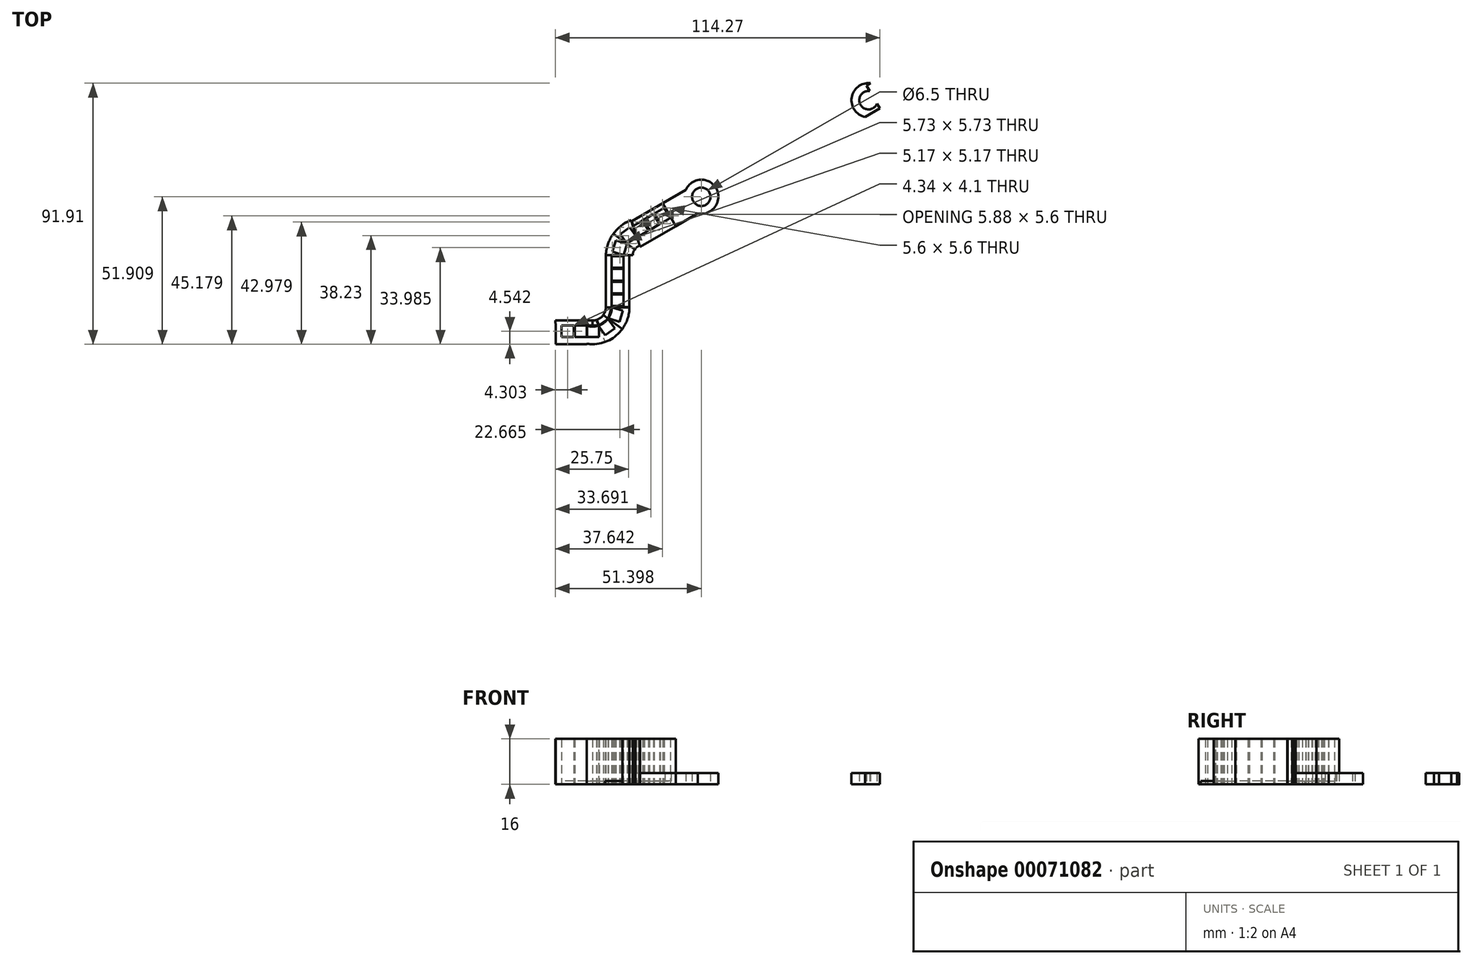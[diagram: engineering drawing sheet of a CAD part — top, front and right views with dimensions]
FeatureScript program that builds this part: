
annotation { "Feature Type Name" : "Feature", "Feature Type Description" : "" }
export const myFeature = defineFeature(function(context is Context, id is Id, definition is map)
    precondition{}
    {
        {
            var Q0;
            Q0=qCreatedBy(makeId("Top.planeOp"),FACE);
            var sketch = newSketch(context, id + "F0", { "sketchPlane" : qUnion([Q0])});
            skArc(sketch, "E0", {"start": v(-24.67, 35.72) * mm, "mid": v(-17.3, 34.42) * mm, "end": v(-13.22, 40.7) * mm});
            skLineSegment(sketch, "E1", {"start": v(-20, 40.64) * mm, "end": v(-26.78, 40.64) * mm});
            skLineSegment(sketch, "E2", {"start": v(-25.5, 44.6) * mm, "end": v(-26.77, 40.7) * mm});
            skLineSegment(sketch, "E3", {"start": v(-26.77, 40.7) * mm, "end": v(-30.67, 41.96) * mm});
            skLineSegment(sketch, "E4", {"start": v(-30.67, 41.96) * mm, "end": v(-29.4, 45.86) * mm});
            skLineSegment(sketch, "E5", {"start": v(-29.4, 45.86) * mm, "end": v(-25.5, 44.6) * mm});
            skArc(sketch, "E6", {"start": v(-23.08, 42.3) * mm, "mid": v(-20.83, 37.24) * mm, "end": v(-16.5, 40.7) * mm});
            skLineSegment(sketch, "E7", {"start": v(-30.9, 40.7) * mm, "end": v(-33, 40.7) * mm});
            skLineSegment(sketch, "E8.bottom", {"start": v(-26.8, 40.64) * mm, "end": v(-13.2, 40.64) * mm});
            skLineSegment(sketch, "E8.top", {"start": v(-26.8, 22.34) * mm, "end": v(-13.2, 22.34) * mm});
            skLineSegment(sketch, "E8.left", {"start": v(-26.8, 40.64) * mm, "end": v(-26.8, 22.34) * mm});
            skLineSegment(sketch, "E8.right", {"start": v(-13.2, 40.64) * mm, "end": v(-13.2, 22.34) * mm});
            skPoint(sketch, "E8.middle", {"position": v(-20, 31.5) * mm});
            skLineSegment(sketch, "E9.top", {"start": v(-30.9, 22.3) * mm, "end": v(-9.1, 22.3) * mm});
            skLineSegment(sketch, "E9.left", {"start": v(-30.9, 40.7) * mm, "end": v(-30.9, 22.3) * mm});
            skLineSegment(sketch, "E9.right", {"start": v(-9.1, 40.7) * mm, "end": v(-9.1, 22.3) * mm});
            skLineSegment(sketch, "E10.bottom", {"start": v(-26.8, 36.2) * mm, "end": v(-30.9, 36.2) * mm});
            skLineSegment(sketch, "E10.top", {"start": v(-26.8, 35.8) * mm, "end": v(-30.9, 35.8) * mm});
            skLineSegment(sketch, "E10.left", {"start": v(-26.8, 36.2) * mm, "end": v(-26.8, 35.8) * mm});
            skLineSegment(sketch, "E10.right", {"start": v(-30.9, 36.2) * mm, "end": v(-30.9, 35.8) * mm});
            skLineSegment(sketch, "E11.bottom", {"start": v(-26.8, 31.7) * mm, "end": v(-30.9, 31.7) * mm});
            skLineSegment(sketch, "E11.top", {"start": v(-26.8, 31.3) * mm, "end": v(-30.9, 31.3) * mm});
            skLineSegment(sketch, "E11.left", {"start": v(-26.8, 31.7) * mm, "end": v(-26.8, 31.3) * mm});
            skLineSegment(sketch, "E11.right", {"start": v(-30.9, 31.7) * mm, "end": v(-30.9, 31.3) * mm});
            skLineSegment(sketch, "E12.bottom", {"start": v(-26.8, 27.2) * mm, "end": v(-30.9, 27.2) * mm});
            skLineSegment(sketch, "E12.top", {"start": v(-26.8, 26.8) * mm, "end": v(-30.9, 26.8) * mm});
            skLineSegment(sketch, "E12.left", {"start": v(-26.8, 27.2) * mm, "end": v(-26.8, 26.8) * mm});
            skLineSegment(sketch, "E12.right", {"start": v(-30.9, 27.2) * mm, "end": v(-30.9, 26.8) * mm});
            skLineSegment(sketch, "E13.bottom", {"start": v(-26.8, 22.7) * mm, "end": v(-30.9, 22.7) * mm});
            skLineSegment(sketch, "E13.top", {"start": v(-26.8, 22.3) * mm, "end": v(-30.9, 22.3) * mm});
            skLineSegment(sketch, "E13.left", {"start": v(-26.8, 22.7) * mm, "end": v(-26.8, 22.3) * mm});
            skLineSegment(sketch, "E13.right", {"start": v(-30.9, 22.7) * mm, "end": v(-30.9, 22.3) * mm});
            skLineSegment(sketch, "E14", {"start": v(-30.9, 22.3) * mm, "end": v(-37.68, 22.3) * mm});
            skArc(sketch, "E15", {"start": v(-33, 27.22) * mm, "mid": v(-43.84, 19.43) * mm, "end": v(-30.9, 22.7) * mm});
            skLineSegment(sketch, "E16", {"start": v(-30.9, 22.3) * mm, "end": v(-32.12, 18.38) * mm});
            skLineSegment(sketch, "E17", {"start": v(-32.12, 18.38) * mm, "end": v(-28.21, 17.15) * mm});
            skLineSegment(sketch, "E18", {"start": v(-28.21, 17.15) * mm, "end": v(-26.98, 21.06) * mm});
            skLineSegment(sketch, "E19", {"start": v(-26.98, 21.06) * mm, "end": v(-30.9, 22.3) * mm});
            skLineSegment(sketch, "E20", {"start": v(-37.68, 22.3) * mm, "end": v(-27.16, 14.65) * mm});
            skLineSegment(sketch, "E21", {"start": v(-33, 40.7) * mm, "end": v(-33, 22.3) * mm});
            skArc(sketch, "E22.trimOffspring", {"start": v(-33, 34.42) * mm, "mid": v(-48.38, 14.92) * mm, "end": v(-24.68, 22.34) * mm});
            skArc(sketch, "E23.trimOffspring", {"start": v(-26.3, 28.84) * mm, "mid": v(-24.94, 28.18) * mm, "end": v(-23.5, 27.7) * mm});
            skLineSegment(sketch, "E24", {"start": v(-33, 40.3) * mm, "end": v(-26.8, 40.3) * mm});
            skLineSegment(sketch, "E25", {"start": v(-26.8, 40.64) * mm, "end": v(-33, 40.64) * mm});
            skArc(sketch, "E26.trimOffspring", {"start": v(-26.8, 40.68) * mm, "mid": v(-26.8, 40.64) * mm, "end": v(-26.8, 40.6) * mm});
            skLineSegment(sketch, "E27.trimOffspring", {"start": v(-23.5, 40.7) * mm, "end": v(-9.1, 40.7) * mm});
            skLineSegment(sketch, "E28", {"start": v(-20, 40.64) * mm, "end": v(-33, 40.7) * mm});
            skLineSegment(sketch, "E29", {"start": v(-20, 40.64) * mm, "end": v(-30.3, 48.13) * mm});
            skLineSegment(sketch, "E30", {"start": v(-23.5, 40.7) * mm, "end": v(-23.5, 22.3) * mm});
            skCircle(sketch, "E31", {"center": v(-37.68, 22.3) * mm, "radius": 4.68 * mm});
            skLineSegment(sketch, "E32", {"start": v(-20, 40.64) * mm, "end": v(-20.07, 22.3) * mm});
            skLineSegment(sketch, "E33", {"start": v(-37.68, 22.3) * mm, "end": v(-37.68, 15.5) * mm});
            skLineSegment(sketch, "E34", {"start": v(-37.64, 9.3) * mm, "end": v(-52.13, 9.3) * mm});
            skLineSegment(sketch, "E35", {"start": v(-50.68, 15.5) * mm, "end": v(-50.68, 9.3) * mm});
            skLineSegment(sketch, "E36.top", {"start": v(-39.78, 11.78) * mm, "end": v(-50.68, 11.78) * mm});
            skLineSegment(sketch, "E36.left", {"start": v(-39.78, 15.5) * mm, "end": v(-39.78, 11.78) * mm});
            skLineSegment(sketch, "E36.right", {"start": v(-50.68, 15.5) * mm, "end": v(-50.68, 11.78) * mm});
            skLineSegment(sketch, "E37.bottom", {"start": v(-43.88, 15.88) * mm, "end": v(-44.28, 15.88) * mm});
            skLineSegment(sketch, "E37.top", {"start": v(-43.88, 11.78) * mm, "end": v(-44.28, 11.78) * mm});
            skLineSegment(sketch, "E37.left", {"start": v(-43.88, 15.88) * mm, "end": v(-43.88, 11.78) * mm});
            skLineSegment(sketch, "E37.right", {"start": v(-44.28, 15.88) * mm, "end": v(-44.28, 11.78) * mm});
            skLineSegment(sketch, "E38.bottom", {"start": v(-49.02, 11.78) * mm, "end": v(-48.62, 11.78) * mm});
            skLineSegment(sketch, "E38.top", {"start": v(-49.02, 15.88) * mm, "end": v(-48.62, 15.88) * mm});
            skLineSegment(sketch, "E38.left", {"start": v(-49.02, 11.78) * mm, "end": v(-49.02, 15.88) * mm});
            skLineSegment(sketch, "E38.right", {"start": v(-48.62, 11.78) * mm, "end": v(-48.62, 15.88) * mm});
            skLineSegment(sketch, "E39", {"start": v(-37.68, 17.61) * mm, "end": v(-39.78, 17.61) * mm});
            skLineSegment(sketch, "E40", {"start": v(-39.78, 17.61) * mm, "end": v(-39.78, 9.3) * mm});
            skLineSegment(sketch, "E41", {"start": v(-37.68, 17.61) * mm, "end": v(-50.75, 17.61) * mm});
            skLineSegment(sketch, "E42", {"start": v(-50.75, 17.61) * mm, "end": v(-50.68, 15.5) * mm});
            skLineSegment(sketch, "E43", {"start": v(-35.42, 15.88) * mm, "end": v(-32.15, 18.35) * mm});
            skLineSegment(sketch, "E44", {"start": v(-35.42, 15.88) * mm, "end": v(-50.68, 15.88) * mm});
            skLineSegment(sketch, "E45.bottom", {"start": v(-35.46, 15.88) * mm, "end": v(-39.56, 15.88) * mm});
            skLineSegment(sketch, "E45.top", {"start": v(-35.46, 11.78) * mm, "end": v(-39.56, 11.78) * mm});
            skLineSegment(sketch, "E45.left", {"start": v(-35.46, 15.88) * mm, "end": v(-35.46, 11.78) * mm});
            skLineSegment(sketch, "E45.right", {"start": v(-39.56, 15.88) * mm, "end": v(-39.56, 11.78) * mm});
            skLineSegment(sketch, "E46", {"start": v(-36.2, 17.85) * mm, "end": v(-35.42, 15.88) * mm});
            skLineSegment(sketch, "E47", {"start": v(-35.42, 15.88) * mm, "end": v(-33.3, 10.05) * mm});
            skArc(sketch, "E48.trimOffspring", {"start": v(-20.05, 27.21) * mm, "mid": v(-10.8, 49.4) * mm, "end": v(-33, 40.2) * mm});
            skLineSegment(sketch, "E49", {"start": v(-20, 40.21) * mm, "end": v(-20, 53.21) * mm});
            skLineSegment(sketch, "E50", {"start": v(-24.68, 22.34) * mm, "end": v(-24.67, 40.64) * mm});
            skLineSegment(sketch, "E51", {"start": v(-20, 40.64) * mm, "end": v(-23.89, 52.62) * mm});
            skLineSegment(sketch, "E52", {"start": v(-25.5, 44.6) * mm, "end": v(-21.94, 46.63) * mm});
            skLineSegment(sketch, "E53", {"start": v(-23.08, 42.3) * mm, "end": v(63.52, 92.3) * mm});
            skLineSegment(sketch, "E54", {"start": v(-23.89, 52.62) * mm, "end": v(114.67, 132.62) * mm});
            skLineSegment(sketch, "E55", {"start": v(63.52, 92.3) * mm, "end": v(58.85, 100.39) * mm});
            skCircle(sketch, "E56", {"center": v(0.65, 61.2) * mm, "radius": 6 * mm});
            skCircle(sketch, "E57", {"center": v(0.65, 61.2) * mm, "radius": 3.25 * mm});
            skCircle(sketch, "E58", {"center": v(59.54, 95.2) * mm, "radius": 6 * mm});
            skCircle(sketch, "E59", {"center": v(59.54, 95.2) * mm, "radius": 3.25 * mm});
            skCircle(sketch, "E60", {"center": v(26.63, 76.2) * mm, "radius": 1.5 * mm});
            skLineSegment(sketch, "E61", {"start": v(-21.57, 47.22) * mm, "end": v(-10.05, 53.87) * mm});
            skLineSegment(sketch, "E62", {"start": v(-10.05, 53.87) * mm, "end": v(-8.3, 50.84) * mm});
            skLineSegment(sketch, "E63", {"start": v(-21.57, 47.22) * mm, "end": v(-23.62, 50.77) * mm});
            skLineSegment(sketch, "E64", {"start": v(-23.62, 50.77) * mm, "end": v(-12.1, 57.42) * mm});
            skLineSegment(sketch, "E65", {"start": v(-12.1, 57.42) * mm, "end": v(-10.05, 53.87) * mm});
            skLineSegment(sketch, "E66", {"start": v(-18.02, 49.27) * mm, "end": v(-20.07, 52.82) * mm});
            skLineSegment(sketch, "E67", {"start": v(-17.67, 49.47) * mm, "end": v(-19.72, 53.02) * mm});
            skLineSegment(sketch, "E68", {"start": v(-13.86, 51.67) * mm, "end": v(-15.9, 55.22) * mm});
            skLineSegment(sketch, "E69", {"start": v(-14.12, 51.52) * mm, "end": v(-16.17, 55.07) * mm});
            skLineSegment(sketch, "E70", {"start": v(-10.3, 53.72) * mm, "end": v(-12.36, 57.27) * mm});
            skLineSegment(sketch, "E71", {"start": v(-10.05, 53.87) * mm, "end": v(-12.1, 57.42) * mm});
            skLineSegment(sketch, "E72", {"start": v(-12.1, 57.42) * mm, "end": v(-12.97, 58.92) * mm});
            skSolve(sketch);
        }
        {
            var Q0;
            Q0=makeQuery(id+"F0.imprint","IMPRINT",FACE,{"disambiguationData":[TD([[makeQuery(id+"F0.imprint","IMPRINT",EDGE,{"derivedFrom":sQuery(id+"F0.wireOp",EDGE,"E2")}),1.0]])]});
            extrude(context, id + "F1", {"entities" : qUnion([Q0]), "depth" : 16 * mm, "offsetDistance" : 25 * mm});
        }
        {
            var Q0;
            {var subQ0=sQuery(id+"F0.wireOp",EDGE,"E9.left");var subQ13=sQuery(id+"F0.wireOp",EDGE,"E24");var subQ14=makeQuery(id+"F0.imprint","INTERSECT",VERTEX,{"derivedFrom":[subQ0,subQ13]});Q0=makeQuery(id+"F0.imprint","IMPRINT",FACE,{"disambiguationData":[TD([[makeQuery(id+"F0.imprint","IMPRINT",EDGE,{"disambiguationData":[TD([[subQ14,-1.0]])],"derivedFrom":subQ0}),-1.0]])]});}
            var Q1;
            {var subQ0=sQuery(id+"F0.wireOp",EDGE,"E8.left");var subQ16=makeQuery(id+"F0.imprint","INTERSECT",VERTEX,{"derivedFrom":[subQ0,sQuery(id+"F0.wireOp",EDGE,"E24")]});Q1=makeQuery(id+"F0.imprint","IMPRINT",FACE,{"disambiguationData":[TD([[makeQuery(id+"F0.imprint","IMPRINT",EDGE,{"disambiguationData":[TD([[subQ16,-1.0]])],"derivedFrom":subQ0}),1.0]])]});}
            var Q2;
            {var subQ4=sQuery(id+"F0.wireOp",EDGE,"E13.bottom");Q2=makeQuery(id+"F0.imprint","IMPRINT",FACE,{"disambiguationData":[TD([[makeQuery(id+"F0.imprint","IMPRINT",EDGE,{"derivedFrom":subQ4}),1.0]])]});}
            var Q3;
            {var subQ0=sQuery(id+"F0.wireOp",EDGE,"E24");var subQ1=sQuery(id+"F0.wireOp",EDGE,"E9.left");var subQ2=makeQuery(id+"F0.imprint","INTERSECT",VERTEX,{"derivedFrom":[subQ1,subQ0]});Q3=makeQuery(id+"F0.imprint","IMPRINT",FACE,{"disambiguationData":[TD([[makeQuery(id+"F0.imprint","IMPRINT",EDGE,{"disambiguationData":[TD([[subQ2,1.0]])],"derivedFrom":subQ1}),-1.0]])]});}
            var Q4;
            {var subQ0=sQuery(id+"F0.wireOp",EDGE,"E28");var subQ1=sQuery(id+"F0.wireOp",EDGE,"E9.left");var subQ2=makeQuery(id+"F0.imprint","INTERSECT",VERTEX,{"derivedFrom":[subQ1,subQ0]});Q4=makeQuery(id+"F0.imprint","IMPRINT",FACE,{"disambiguationData":[TD([[makeQuery(id+"F0.imprint","IMPRINT",EDGE,{"disambiguationData":[TD([[subQ2,-1.0]])],"derivedFrom":subQ1}),-1.0]])]});}
            var Q5;
            {var subQ0=sQuery(id+"F0.wireOp",EDGE,"2WVfRbEO-jWGe-ECgv-KHEP-8MCzaF3kxnAQ");var subQ1=sQuery(id+"F0.wireOp",EDGE,"E1");var subQ2=makeQuery(id+"F0.imprint","INTERSECT",VERTEX,{"derivedFrom":[subQ1,subQ0]});Q5=makeQuery(id+"F0.imprint","IMPRINT",FACE,{"disambiguationData":[TD([[makeQuery(id+"F0.imprint","IMPRINT",EDGE,{"disambiguationData":[TD([[subQ2,-1.0]])],"derivedFrom":subQ0}),1.0]])]});}
            var Q6;
            {var subQ0=sQuery(id+"F0.wireOp",EDGE,"E7");Q6=makeQuery(id+"F0.imprint","IMPRINT",FACE,{"disambiguationData":[TD([[makeQuery(id+"F0.imprint","IMPRINT",EDGE,{"derivedFrom":subQ0}),1.0]])]});}
            var Q7;
            {var subQ5=sQuery(id+"F0.wireOp",EDGE,"E53");var subQ7=sQuery(id+"F0.wireOp",EDGE,"E48.trimOffspring");var subQ8=makeQuery(id+"F0.imprint","INTERSECT",VERTEX,{"derivedFrom":[subQ7,subQ5]});Q7=makeQuery(id+"F0.imprint","IMPRINT",FACE,{"disambiguationData":[TD([[makeQuery(id+"F0.imprint","IMPRINT",EDGE,{"disambiguationData":[TD([[subQ8,-1.0]])],"derivedFrom":subQ7}),1.0]])]});}
            var Q8;
            {var subQ0=sQuery(id+"F0.wireOp",EDGE,"E72");Q8=makeQuery(id+"F0.imprint","IMPRINT",FACE,{"disambiguationData":[TD([[makeQuery(id+"F0.imprint","IMPRINT",EDGE,{"derivedFrom":subQ0}),1.0]])]});}
            var Q9;
            {var subQ0=sQuery(id+"F0.wireOp",EDGE,"E62");Q9=makeQuery(id+"F0.imprint","IMPRINT",FACE,{"disambiguationData":[TD([[makeQuery(id+"F0.imprint","IMPRINT",EDGE,{"derivedFrom":subQ0}),-1.0]])]});}
            var Q10;
            {var subQ0=sQuery(id+"F0.wireOp",EDGE,"E49");var subQ1=sQuery(id+"F0.wireOp",EDGE,"E48.trimOffspring");var subQ2=makeQuery(id+"F0.imprint","INTERSECT",VERTEX,{"derivedFrom":[subQ1,subQ0]});Q10=makeQuery(id+"F0.imprint","IMPRINT",FACE,{"disambiguationData":[TD([[makeQuery(id+"F0.imprint","IMPRINT",EDGE,{"disambiguationData":[TD([[subQ2,1.0]])],"derivedFrom":subQ0}),1.0]])]});}
            var Q11;
            {var subQ2=sQuery(id+"F0.wireOp",EDGE,"E66");Q11=makeQuery(id+"F0.imprint","IMPRINT",FACE,{"disambiguationData":[TD([[makeQuery(id+"F0.imprint","IMPRINT",EDGE,{"derivedFrom":subQ2}),-1.0]])]});}
            var Q12;
            {var subQ0=sQuery(id+"F0.wireOp",EDGE,"E65");Q12=makeQuery(id+"F0.imprint","IMPRINT",FACE,{"disambiguationData":[TD([[makeQuery(id+"F0.imprint","IMPRINT",EDGE,{"derivedFrom":subQ0}),-1.0]])]});}
            var Q13;
            {var subQ0=sQuery(id+"F0.wireOp",EDGE,"E68");var subQ1=sQuery(id+"F0.wireOp",EDGE,"E48.trimOffspring");var subQ2=makeQuery(id+"F0.imprint","INTERSECT",VERTEX,{"derivedFrom":[subQ1,subQ0]});Q13=makeQuery(id+"F0.imprint","IMPRINT",FACE,{"disambiguationData":[TD([[makeQuery(id+"F0.imprint","IMPRINT",EDGE,{"disambiguationData":[TD([[subQ2,-1.0]])],"derivedFrom":subQ1}),-1.0]])]});}
            var Q14;
            {var subQ0=sQuery(id+"F0.wireOp",EDGE,"E68");var subQ1=sQuery(id+"F0.wireOp",EDGE,"E48.trimOffspring");var subQ2=makeQuery(id+"F0.imprint","INTERSECT",VERTEX,{"derivedFrom":[subQ1,subQ0]});Q14=makeQuery(id+"F0.imprint","IMPRINT",FACE,{"disambiguationData":[TD([[makeQuery(id+"F0.imprint","IMPRINT",EDGE,{"disambiguationData":[TD([[subQ2,-1.0]])],"derivedFrom":subQ1}),1.0]])]});}
            var Q15;
            {var subQ6=sQuery(id+"F0.wireOp",EDGE,"E49");var subQ8=sQuery(id+"F0.wireOp",EDGE,"E61");var subQ10=makeQuery(id+"F0.imprint","INTERSECT",VERTEX,{"derivedFrom":[subQ6,subQ8]});Q15=makeQuery(id+"F0.imprint","IMPRINT",FACE,{"disambiguationData":[TD([[makeQuery(id+"F0.imprint","IMPRINT",EDGE,{"disambiguationData":[TD([[subQ10,1.0]])],"derivedFrom":subQ6}),1.0]])]});}
            var Q16;
            {var subQ7=sQuery(id+"F0.wireOp",EDGE,"E67");Q16=makeQuery(id+"F0.imprint","IMPRINT",FACE,{"disambiguationData":[TD([[makeQuery(id+"F0.imprint","IMPRINT",EDGE,{"derivedFrom":subQ7}),1.0]])]});}
            extrude(context, id + "F2", {"entities" : qUnion([Q0, Q1, Q2, Q3, Q4, Q5, Q6, Q7, Q8, Q9, Q10, Q11, Q12, Q13, Q14, Q15, Q16]), "depth" : 16 * mm, "offsetDistance" : 25 * mm});
        }
        {
            var Q0;
            {var subQ0=sQuery(id+"F0.wireOp",EDGE,"E10.bottom");Q0=makeQuery(id+"F0.imprint","IMPRINT",FACE,{"disambiguationData":[TD([[makeQuery(id+"F0.imprint","IMPRINT",EDGE,{"derivedFrom":subQ0}),1.0]])]});}
            var Q1;
            {var subQ2=sQuery(id+"F0.wireOp",EDGE,"E8.left");var subQ6=sQuery(id+"F0.wireOp",EDGE,"E24");var subQ7=makeQuery(id+"F0.imprint","INTERSECT",VERTEX,{"derivedFrom":[subQ2,subQ6]});Q1=makeQuery(id+"F0.imprint","IMPRINT",FACE,{"disambiguationData":[TD([[makeQuery(id+"F0.imprint","IMPRINT",EDGE,{"disambiguationData":[TD([[subQ7,1.0]])],"derivedFrom":subQ2}),-1.0]])]});}
            var Q2;
            {var subQ0=sQuery(id+"F0.wireOp",EDGE,"E11.bottom");Q2=makeQuery(id+"F0.imprint","IMPRINT",FACE,{"disambiguationData":[TD([[makeQuery(id+"F0.imprint","IMPRINT",EDGE,{"derivedFrom":subQ0}),1.0]])]});}
            var Q3;
            {var subQ0=sQuery(id+"F0.wireOp",EDGE,"E12.bottom");Q3=makeQuery(id+"F0.imprint","IMPRINT",FACE,{"disambiguationData":[TD([[makeQuery(id+"F0.imprint","IMPRINT",EDGE,{"derivedFrom":subQ0}),1.0]])]});}
            extrude(context, id + "F3", {"entities" : qUnion([Q0, Q1, Q2, Q3]), "depth" : 16 * mm, "offsetDistance" : 25 * mm});
        }
        {
            var Q0;
            {var subQ9=sQuery(id+"F0.wireOp",EDGE,"E17");Q0=makeQuery(id+"F0.imprint","IMPRINT",FACE,{"disambiguationData":[TD([[makeQuery(id+"F0.imprint","IMPRINT",EDGE,{"derivedFrom":subQ9}),-1.0]])]});}
            var Q1;
            {var subQ5=sQuery(id+"F0.wireOp",EDGE,"E16");Q1=makeQuery(id+"F0.imprint","IMPRINT",FACE,{"disambiguationData":[TD([[makeQuery(id+"F0.imprint","IMPRINT",EDGE,{"derivedFrom":subQ5}),-1.0]])]});}
            extrude(context, id + "F4", {"entities" : qUnion([Q0, Q1]), "depth" : 16 * mm, "offsetDistance" : 25 * mm});
        }
        {
            var Q0;
            Q0=makeQuery(id+"F1.opExtrude","SWEPT_BODY",BODY,{"disambiguationData":[OSD([sQuery(id+"F0.wireOp",EDGE,"E2"),sQuery(id+"F0.wireOp",EDGE,"E3"),sQuery(id+"F0.wireOp",EDGE,"E4"),sQuery(id+"F0.wireOp",EDGE,"E5"),sQuery(id+"F0.wireOp",EDGE,"E6"),sQuery(id+"F0.wireOp",EDGE,"E7"),sQuery(id+"F0.wireOp",EDGE,"E9.left"),sQuery(id+"F0.wireOp",EDGE,"E23.trimOffspring"),sQuery(id+"F0.wireOp",EDGE,"E28"),sQuery(id+"F0.wireOp",EDGE,"E29")])]});
            var Q1;
            Q1=makeQuery(id+"F1.opExtrude","SWEPT_FACE",FACE,{"disambiguationData":[OSD([sQuery(id+"F0.wireOp",EDGE,"E29")])]});
            mirror(context, id + "F5", {"entities" : qUnion([Q0]), "mirrorPlane" : qUnion([Q1])});
        }
        {
            var Q0;
            Q0=makeQuery(id+"F4.opExtrude","SWEPT_BODY",BODY,{"disambiguationData":[OSD([sQuery(id+"F0.wireOp",EDGE,"E9.top"),sQuery(id+"F0.wireOp",EDGE,"E14"),sQuery(id+"F0.wireOp",EDGE,"E15"),sQuery(id+"F0.wireOp",EDGE,"E16"),sQuery(id+"F0.wireOp",EDGE,"E17"),sQuery(id+"F0.wireOp",EDGE,"E18"),sQuery(id+"F0.wireOp",EDGE,"E19"),sQuery(id+"F0.wireOp",EDGE,"E20"),sQuery(id+"F0.wireOp",EDGE,"E22.trimOffspring"),sQuery(id+"F0.wireOp",EDGE,"E31")])]});
            var Q1;
            Q1=makeQuery(id+"F4.opExtrude","SWEPT_FACE",FACE,{"disambiguationData":[OSD([sQuery(id+"F0.wireOp",EDGE,"E20")])]});
            mirror(context, id + "F6", {"entities" : qUnion([Q0]), "mirrorPlane" : qUnion([Q1])});
        }
        {
            var Q0;
            {var subQ3=sQuery(id+"F0.wireOp",EDGE,"E40");var subQ5=sQuery(id+"F0.wireOp",EDGE,"E22.trimOffspring");var subQ7=makeQuery(id+"F0.imprint","INTERSECT",VERTEX,{"derivedFrom":[subQ5,subQ3]});Q0=makeQuery(id+"F0.imprint","IMPRINT",FACE,{"disambiguationData":[TD([[makeQuery(id+"F0.imprint","IMPRINT",EDGE,{"disambiguationData":[TD([[subQ7,1.0]])],"derivedFrom":subQ5}),1.0]])]});}
            var Q1;
            {var subQ2=sQuery(id+"F0.wireOp",EDGE,"E22.trimOffspring");var subQ8=sQuery(id+"F0.wireOp",EDGE,"E40");var subQ10=makeQuery(id+"F0.imprint","INTERSECT",VERTEX,{"derivedFrom":[subQ2,subQ8]});Q1=makeQuery(id+"F0.imprint","IMPRINT",FACE,{"disambiguationData":[TD([[makeQuery(id+"F0.imprint","IMPRINT",EDGE,{"disambiguationData":[TD([[subQ10,1.0]])],"derivedFrom":subQ2}),-1.0]])]});}
            var Q2;
            {var subQ3=sQuery(id+"F0.wireOp",EDGE,"E38.left");Q2=makeQuery(id+"F0.imprint","IMPRINT",FACE,{"disambiguationData":[TD([[makeQuery(id+"F0.imprint","IMPRINT",EDGE,{"derivedFrom":subQ3}),1.0]])]});}
            var Q3;
            {var subQ0=sQuery(id+"F0.wireOp",EDGE,"E42");Q3=makeQuery(id+"F0.imprint","IMPRINT",FACE,{"disambiguationData":[TD([[makeQuery(id+"F0.imprint","IMPRINT",EDGE,{"derivedFrom":subQ0}),1.0]])]});}
            var Q4;
            {var subQ0=sQuery(id+"F0.wireOp",EDGE,"E41");var subQ1=sQuery(id+"F0.wireOp",EDGE,"E15");var subQ2=makeQuery(id+"F0.imprint","INTERSECT",VERTEX,{"derivedFrom":[subQ1,subQ0]});Q4=makeQuery(id+"F0.imprint","IMPRINT",FACE,{"disambiguationData":[TD([[makeQuery(id+"F0.imprint","IMPRINT",EDGE,{"disambiguationData":[TD([[subQ2,-1.0]])],"derivedFrom":subQ1}),1.0]])]});}
            var Q5;
            {var subQ2=sQuery(id+"F0.wireOp",EDGE,"E37.left");Q5=makeQuery(id+"F0.imprint","IMPRINT",FACE,{"disambiguationData":[TD([[makeQuery(id+"F0.imprint","IMPRINT",EDGE,{"derivedFrom":subQ2}),-1.0]])]});}
            var Q6;
            {var subQ0=sQuery(id+"F0.wireOp",EDGE,"E38.left");Q6=makeQuery(id+"F0.imprint","IMPRINT",FACE,{"disambiguationData":[TD([[makeQuery(id+"F0.imprint","IMPRINT",EDGE,{"derivedFrom":subQ0}),-1.0]])]});}
            var Q7;
            {var subQ10=sQuery(id+"F0.wireOp",EDGE,"E36.left");Q7=makeQuery(id+"F0.imprint","IMPRINT",FACE,{"disambiguationData":[TD([[makeQuery(id+"F0.imprint","IMPRINT",EDGE,{"derivedFrom":subQ10}),1.0]])]});}
            var Q8;
            {var subQ5=sQuery(id+"F0.wireOp",EDGE,"E39");Q8=makeQuery(id+"F0.imprint","IMPRINT",FACE,{"disambiguationData":[TD([[makeQuery(id+"F0.imprint","IMPRINT",EDGE,{"derivedFrom":subQ5}),1.0]])]});}
            var Q9;
            {var subQ0=sQuery(id+"F0.wireOp",EDGE,"E41");var subQ1=sQuery(id+"F0.wireOp",EDGE,"E15");var subQ2=makeQuery(id+"F0.imprint","INTERSECT",VERTEX,{"derivedFrom":[subQ1,subQ0]});Q9=makeQuery(id+"F0.imprint","IMPRINT",FACE,{"disambiguationData":[TD([[makeQuery(id+"F0.imprint","IMPRINT",EDGE,{"disambiguationData":[TD([[subQ2,-1.0]])],"derivedFrom":subQ1}),-1.0]])]});}
            var Q10;
            {var subQ0=sQuery(id+"F0.wireOp",EDGE,"E38.top");var subQ1=sQuery(id+"F0.wireOp",EDGE,"E22.trimOffspring");var subQ2=makeQuery(id+"F0.imprint","INTERSECT",VERTEX,{"derivedFrom":[subQ1,subQ0]});Q10=makeQuery(id+"F0.imprint","IMPRINT",FACE,{"disambiguationData":[TD([[makeQuery(id+"F0.imprint","IMPRINT",EDGE,{"disambiguationData":[TD([[subQ2,-1.0]])],"derivedFrom":subQ1}),1.0]])]});}
            extrude(context, id + "F7", {"entities" : qUnion([Q0, Q1, Q2, Q3, Q4, Q5, Q6, Q7, Q8, Q9, Q10]), "operationType" : NewBodyOperationType.ADD, "depth" : 16 * mm, "offsetDistance" : 25 * mm});
        }
        {
            var Q0;
            {var subQ0=sQuery(id+"F0.wireOp",EDGE,"E46");Q0=makeQuery(id+"F0.imprint","IMPRINT",FACE,{"disambiguationData":[TD([[makeQuery(id+"F0.imprint","IMPRINT",EDGE,{"derivedFrom":subQ0}),-1.0]])]});}
            extrude(context, id + "F8", {"entities" : qUnion([Q0]), "depth" : 16 * mm, "offsetDistance" : 25 * mm});
        }
        {
            var Q0;
            {var subQ1=sQuery(id+"F0.wireOp",EDGE,"E48.trimOffspring");var subQ6=sQuery(id+"F0.wireOp",EDGE,"E53");var subQ7=makeQuery(id+"F0.imprint","INTERSECT",VERTEX,{"derivedFrom":[subQ1,subQ6]});Q0=makeQuery(id+"F0.imprint","IMPRINT",FACE,{"disambiguationData":[TD([[makeQuery(id+"F0.imprint","IMPRINT",EDGE,{"disambiguationData":[TD([[subQ7,-1.0]])],"derivedFrom":subQ1}),-1.0]])]});}
            var Q1;
            {var subQ0=sQuery(id+"F0.wireOp",EDGE,"E53");var subQ1=sQuery(id+"F0.wireOp",EDGE,"E48.trimOffspring");var subQ2=makeQuery(id+"F0.imprint","INTERSECT",VERTEX,{"derivedFrom":[subQ1,subQ0]});Q1=makeQuery(id+"F0.imprint","IMPRINT",FACE,{"disambiguationData":[TD([[makeQuery(id+"F0.imprint","IMPRINT",EDGE,{"disambiguationData":[TD([[subQ2,-1.0]])],"derivedFrom":subQ1}),1.0]])]});}
            var Q2;
            {var subQ4=sQuery(id+"F0.wireOp",EDGE,"E53");var subQ5=sQuery(id+"F0.wireOp",EDGE,"E49");var subQ6=makeQuery(id+"F0.imprint","INTERSECT",VERTEX,{"derivedFrom":[subQ5,subQ4]});Q2=makeQuery(id+"F0.imprint","IMPRINT",FACE,{"disambiguationData":[TD([[makeQuery(id+"F0.imprint","IMPRINT",EDGE,{"disambiguationData":[TD([[subQ6,-1.0]])],"derivedFrom":subQ5}),1.0]])]});}
            var Q3;
            {var subQ0=sQuery(id+"F0.wireOp",EDGE,"E56");var subQ3=makeQuery(id+"F0.imprint","IMPRINT",VERTEX,{"derivedFrom":subQ0});Q3=makeQuery(id+"F0.imprint","IMPRINT",FACE,{"disambiguationData":[TD([[makeQuery(id+"F0.imprint","IMPRINT",EDGE,{"disambiguationData":[TD([[subQ3,-1.0]])],"derivedFrom":subQ0}),-1.0]])]});}
            var Q4;
            {var subQ0=sQuery(id+"F0.wireOp",EDGE,"E55");var subQ8=sQuery(id+"F0.wireOp",EDGE,"E53");var subQ9=makeQuery(id+"F0.imprint","INTERSECT",VERTEX,{"derivedFrom":[subQ8,subQ0]});Q4=makeQuery(id+"F0.imprint","IMPRINT",FACE,{"disambiguationData":[TD([[makeQuery(id+"F0.imprint","IMPRINT",EDGE,{"disambiguationData":[TD([[subQ9,1.0]])],"derivedFrom":subQ8}),1.0]])]});}
            var Q5;
            Q5=makeQuery(id+"F0.imprint","IMPRINT",FACE,{"disambiguationData":[TD([[makeQuery(id+"F0.imprint","IMPRINT",EDGE,{"derivedFrom":sQuery(id+"F0.wireOp",EDGE,"E57")}),-1.0]])]});
            var Q6;
            {var subQ0=sQuery(id+"F0.wireOp",EDGE,"E56");var subQ1=sQuery(id+"F0.wireOp",EDGE,"E53");var subQ2=makeQuery(id+"F0.imprint","INTERSECT",VERTEX,{"disambiguationData":[OD(0.0)],"derivedFrom":[subQ1,subQ0]});Q6=makeQuery(id+"F0.imprint","IMPRINT",FACE,{"disambiguationData":[TD([[makeQuery(id+"F0.imprint","IMPRINT",EDGE,{"disambiguationData":[TD([[subQ2,1.0]])],"derivedFrom":subQ1}),-1.0]])]});}
            var Q7;
            {var subQ0=sQuery(id+"F0.wireOp",EDGE,"E56");var subQ1=sQuery(id+"F0.wireOp",EDGE,"E54");var subQ2=makeQuery(id+"F0.imprint","INTERSECT",VERTEX,{"disambiguationData":[OD(0.0)],"derivedFrom":[subQ1,subQ0]});Q7=makeQuery(id+"F0.imprint","IMPRINT",FACE,{"disambiguationData":[TD([[makeQuery(id+"F0.imprint","IMPRINT",EDGE,{"disambiguationData":[TD([[subQ2,-1.0]])],"derivedFrom":subQ1}),1.0]])]});}
            var Q8;
            {var subQ3=sQuery(id+"F0.wireOp",EDGE,"E59");var subQ5=makeQuery(id+"F0.imprint","IMPRINT",VERTEX,{"derivedFrom":subQ3});Q8=makeQuery(id+"F0.imprint","IMPRINT",FACE,{"disambiguationData":[TD([[makeQuery(id+"F0.imprint","IMPRINT",EDGE,{"disambiguationData":[TD([[subQ5,-1.0]])],"derivedFrom":subQ3}),-1.0]])]});}
            var Q9;
            {var subQ0=sQuery(id+"F0.wireOp",EDGE,"E58");var subQ1=sQuery(id+"F0.wireOp",EDGE,"E54");var subQ2=makeQuery(id+"F0.imprint","INTERSECT",VERTEX,{"disambiguationData":[OD(1.0)],"derivedFrom":[subQ1,subQ0]});Q9=makeQuery(id+"F0.imprint","IMPRINT",FACE,{"disambiguationData":[TD([[makeQuery(id+"F0.imprint","IMPRINT",EDGE,{"disambiguationData":[TD([[subQ2,-1.0]])],"derivedFrom":subQ1}),1.0]])]});}
            var Q10;
            {var subQ0=sQuery(id+"F0.wireOp",EDGE,"E62");Q10=makeQuery(id+"F0.imprint","IMPRINT",FACE,{"disambiguationData":[TD([[makeQuery(id+"F0.imprint","IMPRINT",EDGE,{"derivedFrom":subQ0}),1.0]])]});}
            var Q11;
            {var subQ0=sQuery(id+"F0.wireOp",EDGE,"E72");Q11=makeQuery(id+"F0.imprint","IMPRINT",FACE,{"disambiguationData":[TD([[makeQuery(id+"F0.imprint","IMPRINT",EDGE,{"derivedFrom":subQ0}),1.0]])]});}
            var Q12;
            {var subQ0=sQuery(id+"F0.wireOp",EDGE,"E49");var subQ1=sQuery(id+"F0.wireOp",EDGE,"E48.trimOffspring");var subQ2=makeQuery(id+"F0.imprint","INTERSECT",VERTEX,{"derivedFrom":[subQ1,subQ0]});Q12=makeQuery(id+"F0.imprint","IMPRINT",FACE,{"disambiguationData":[TD([[makeQuery(id+"F0.imprint","IMPRINT",EDGE,{"disambiguationData":[TD([[subQ2,1.0]])],"derivedFrom":subQ0}),1.0]])]});}
            var Q13;
            {var subQ3=sQuery(id+"F0.wireOp",EDGE,"E48.trimOffspring");var subQ5=sQuery(id+"F0.wireOp",EDGE,"E49");var subQ6=makeQuery(id+"F0.imprint","INTERSECT",VERTEX,{"derivedFrom":[subQ3,subQ5]});Q13=makeQuery(id+"F0.imprint","IMPRINT",FACE,{"disambiguationData":[TD([[makeQuery(id+"F0.imprint","IMPRINT",EDGE,{"disambiguationData":[TD([[subQ6,1.0]])],"derivedFrom":subQ3}),1.0]])]});}
            var Q14;
            {var subQ0=sQuery(id+"F0.wireOp",EDGE,"E56");var subQ1=sQuery(id+"F0.wireOp",EDGE,"E54");var subQ2=makeQuery(id+"F0.imprint","INTERSECT",VERTEX,{"disambiguationData":[OD(0.0)],"derivedFrom":[subQ1,subQ0]});Q14=makeQuery(id+"F0.imprint","IMPRINT",FACE,{"disambiguationData":[TD([[makeQuery(id+"F0.imprint","IMPRINT",EDGE,{"disambiguationData":[TD([[subQ2,1.0]])],"derivedFrom":subQ1}),1.0]])]});}
            extrude(context, id + "F9", {"entities" : qUnion([Q0, Q1, Q2, Q3, Q4, Q5, Q6, Q7, Q8, Q9, Q10, Q11, Q12, Q13, Q14]), "depth" : 4 * mm, "offsetDistance" : 25 * mm});
        }
        {
            var Q0;
            {var subQ5=sQuery(id+"F0.wireOp",EDGE,"E70");Q0=makeQuery(id+"F0.imprint","IMPRINT",FACE,{"disambiguationData":[TD([[makeQuery(id+"F0.imprint","IMPRINT",EDGE,{"derivedFrom":subQ5}),1.0]])]});}
            var Q1;
            {var subQ0=sQuery(id+"F0.wireOp",EDGE,"E67");Q1=makeQuery(id+"F0.imprint","IMPRINT",FACE,{"disambiguationData":[TD([[makeQuery(id+"F0.imprint","IMPRINT",EDGE,{"derivedFrom":subQ0}),-1.0]])]});}
            var Q2;
            {var subQ0=sQuery(id+"F0.wireOp",EDGE,"E69");var subQ1=sQuery(id+"F0.wireOp",EDGE,"E48.trimOffspring");var subQ2=makeQuery(id+"F0.imprint","INTERSECT",VERTEX,{"derivedFrom":[subQ1,subQ0]});Q2=makeQuery(id+"F0.imprint","IMPRINT",FACE,{"disambiguationData":[TD([[makeQuery(id+"F0.imprint","IMPRINT",EDGE,{"disambiguationData":[TD([[subQ2,-1.0]])],"derivedFrom":subQ1}),-1.0]])]});}
            var Q3;
            {var subQ0=sQuery(id+"F0.wireOp",EDGE,"E61");var subQ1=sQuery(id+"F0.wireOp",EDGE,"E49");var subQ2=makeQuery(id+"F0.imprint","INTERSECT",VERTEX,{"derivedFrom":[subQ1,subQ0]});Q3=makeQuery(id+"F0.imprint","IMPRINT",FACE,{"disambiguationData":[TD([[makeQuery(id+"F0.imprint","IMPRINT",EDGE,{"disambiguationData":[TD([[subQ2,-1.0]])],"derivedFrom":subQ1}),1.0]])]});}
            var Q4;
            {var subQ0=sQuery(id+"F0.wireOp",EDGE,"E61");var subQ1=sQuery(id+"F0.wireOp",EDGE,"E49");var subQ2=makeQuery(id+"F0.imprint","INTERSECT",VERTEX,{"derivedFrom":[subQ1,subQ0]});Q4=makeQuery(id+"F0.imprint","IMPRINT",FACE,{"disambiguationData":[TD([[makeQuery(id+"F0.imprint","IMPRINT",EDGE,{"disambiguationData":[TD([[subQ2,-1.0]])],"derivedFrom":subQ1}),-1.0]])]});}
            var Q5;
            {var subQ5=sQuery(id+"F0.wireOp",EDGE,"E29");var subQ7=sQuery(id+"F0.wireOp",EDGE,"E52");var subQ11=makeQuery(id+"F0.imprint","INTERSECT",VERTEX,{"derivedFrom":[subQ5,subQ7]});Q5=makeQuery(id+"F0.imprint","IMPRINT",FACE,{"disambiguationData":[TD([[makeQuery(id+"F0.imprint","IMPRINT",EDGE,{"disambiguationData":[TD([[subQ11,-1.0]])],"derivedFrom":subQ5}),-1.0]])]});}
            var Q6;
            Q6=makeQuery(id+"F0.imprint","IMPRINT",FACE,{"disambiguationData":[TD([[makeQuery(id+"F0.imprint","IMPRINT",EDGE,{"derivedFrom":sQuery(id+"F0.wireOp",EDGE,"E2")}),-1.0]])]});
            var Q7;
            {var subQ3=sQuery(id+"F0.wireOp",EDGE,"E10.bottom");Q7=makeQuery(id+"F0.imprint","IMPRINT",FACE,{"disambiguationData":[TD([[makeQuery(id+"F0.imprint","IMPRINT",EDGE,{"derivedFrom":subQ3}),-1.0]])]});}
            var Q8;
            {var subQ0=sQuery(id+"F0.wireOp",EDGE,"E10.top");Q8=makeQuery(id+"F0.imprint","IMPRINT",FACE,{"disambiguationData":[TD([[makeQuery(id+"F0.imprint","IMPRINT",EDGE,{"derivedFrom":subQ0}),1.0]])]});}
            var Q9;
            {var subQ0=sQuery(id+"F0.wireOp",EDGE,"E11.top");Q9=makeQuery(id+"F0.imprint","IMPRINT",FACE,{"disambiguationData":[TD([[makeQuery(id+"F0.imprint","IMPRINT",EDGE,{"derivedFrom":subQ0}),1.0]])]});}
            var Q10;
            {var subQ0=sQuery(id+"F0.wireOp",EDGE,"E12.top");Q10=makeQuery(id+"F0.imprint","IMPRINT",FACE,{"disambiguationData":[TD([[makeQuery(id+"F0.imprint","IMPRINT",EDGE,{"derivedFrom":subQ0}),1.0]])]});}
            var Q11;
            {var subQ3=sQuery(id+"F0.wireOp",EDGE,"E17");Q11=makeQuery(id+"F0.imprint","IMPRINT",FACE,{"disambiguationData":[TD([[makeQuery(id+"F0.imprint","IMPRINT",EDGE,{"derivedFrom":subQ3}),1.0]])]});}
            var Q12;
            {var subQ3=sQuery(id+"F0.wireOp",EDGE,"E47");Q12=makeQuery(id+"F0.imprint","IMPRINT",FACE,{"disambiguationData":[TD([[makeQuery(id+"F0.imprint","IMPRINT",EDGE,{"derivedFrom":subQ3}),1.0]])]});}
            var Q13;
            {var subQ0=sQuery(id+"F0.wireOp",EDGE,"E45.top");Q13=makeQuery(id+"F0.imprint","IMPRINT",FACE,{"disambiguationData":[TD([[makeQuery(id+"F0.imprint","IMPRINT",EDGE,{"derivedFrom":subQ0}),-1.0]])]});}
            var Q14;
            {var subQ0=sQuery(id+"F0.wireOp",EDGE,"E36.left");Q14=makeQuery(id+"F0.imprint","IMPRINT",FACE,{"disambiguationData":[TD([[makeQuery(id+"F0.imprint","IMPRINT",EDGE,{"derivedFrom":subQ0}),-1.0]])]});}
            var Q15;
            {var subQ0=sQuery(id+"F0.wireOp",EDGE,"E37.right");Q15=makeQuery(id+"F0.imprint","IMPRINT",FACE,{"disambiguationData":[TD([[makeQuery(id+"F0.imprint","IMPRINT",EDGE,{"derivedFrom":subQ0}),-1.0]])]});}
            var Q16;
            {var subQ0=sQuery(id+"F0.wireOp",EDGE,"E38.right");var subQ1=sQuery(id+"F0.wireOp",EDGE,"E22.trimOffspring");var subQ2=makeQuery(id+"F0.imprint","INTERSECT",VERTEX,{"derivedFrom":[subQ1,subQ0]});Q16=makeQuery(id+"F0.imprint","IMPRINT",FACE,{"disambiguationData":[TD([[makeQuery(id+"F0.imprint","IMPRINT",EDGE,{"disambiguationData":[TD([[subQ2,-1.0]])],"derivedFrom":subQ1}),-1.0]])]});}
            extrude(context, id + "F10", {"entities" : qUnion([Q0, Q1, Q2, Q3, Q4, Q5, Q6, Q7, Q8, Q9, Q10, Q11, Q12, Q13, Q14, Q15, Q16]), "depth" : 1.2 * mm, "offsetDistance" : 25 * mm});
        }
    });
